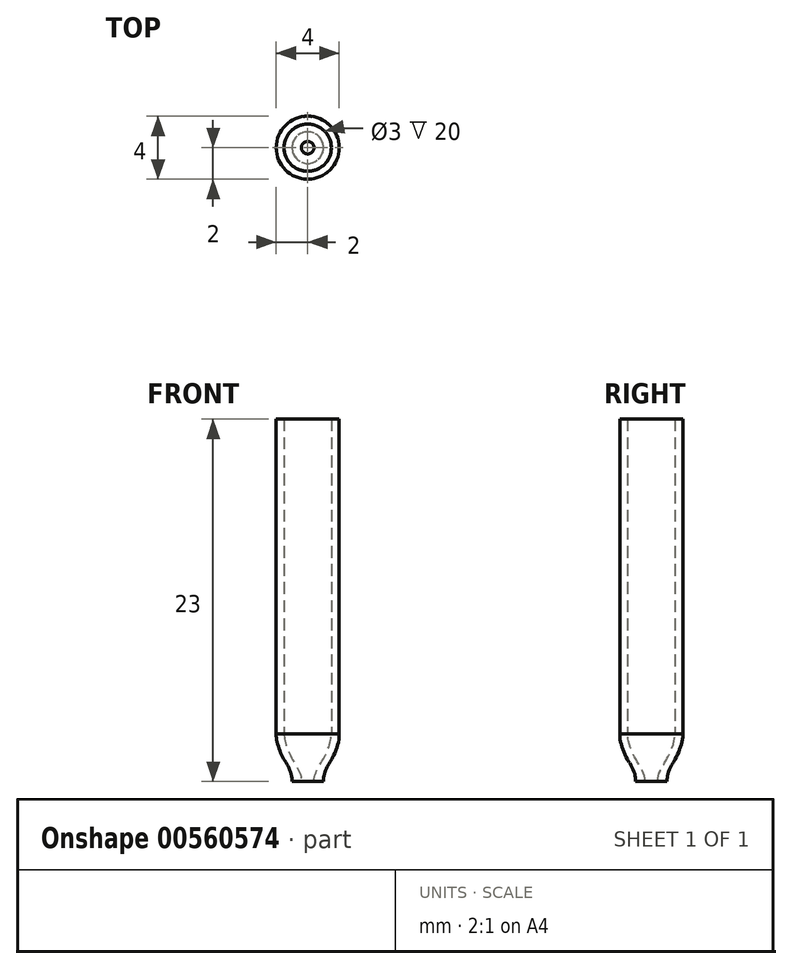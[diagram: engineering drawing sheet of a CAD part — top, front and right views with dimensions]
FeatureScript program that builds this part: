
annotation { "Feature Type Name" : "Feature", "Feature Type Description" : "" }
export const myFeature = defineFeature(function(context is Context, id is Id, definition is map)
    precondition{}
    {
        {
            var Q0;
            Q0=qCreatedBy(makeId("Front.planeOp"),FACE);
            var sketch = newSketch(context, id + "F0", { "sketchPlane" : qUnion([Q0])});
            skLineSegment(sketch, "E0", {"start": v(-1.5, 20) * mm, "end": v(-2, 20) * mm});
            skLineSegment(sketch, "E1", {"start": v(-2, 20) * mm, "end": v(-2, 0) * mm});
            skLineSegment(sketch, "E2", {"start": v(-1.5, 20) * mm, "end": v(-1.5, 0) * mm});
            skFitSpline(sketch, "E3", {"points": [v(-1.5, 0) * mm, v(-1.13, -1.32) * mm, v(-0.4, -3) * mm], "startDerivative": vector(0, -2.07) * mm, "endDerivative": vector(0.02, -3.35) * mm});
            skFitSpline(sketch, "E4", {"points": [v(-2, 0) * mm, v(-1.56, -1.52) * mm, v(-1, -3) * mm], "startDerivative": vector(-0.09, -2.54) * mm, "endDerivative": vector(0, -4.2) * mm});
            skLineSegment(sketch, "E5", {"start": v(-2.98, -3) * mm, "end": v(2.18, -3) * mm, "construction": true});
            skLineSegment(sketch, "E6", {"start": v(-1, -3) * mm, "end": v(-0.4, -3) * mm});
            skLineSegment(sketch, "E7", {"start": v(0, -7.5) * mm, "end": v(0, 24.93) * mm, "construction": true});
            skSolve(sketch);
        }
        {
            var Q0;
            Q0 = qSketchRegion(id + "F0", true);
            var Q1;
            Q1=sQuery(id+"F0.wireOp",EDGE,"E7");
            revolve(context, id + "F1", {"entities" : qUnion([Q0]), "axis" : qUnion([Q1]), "revolveType" : RevolveType.FULL});
        }
    });
